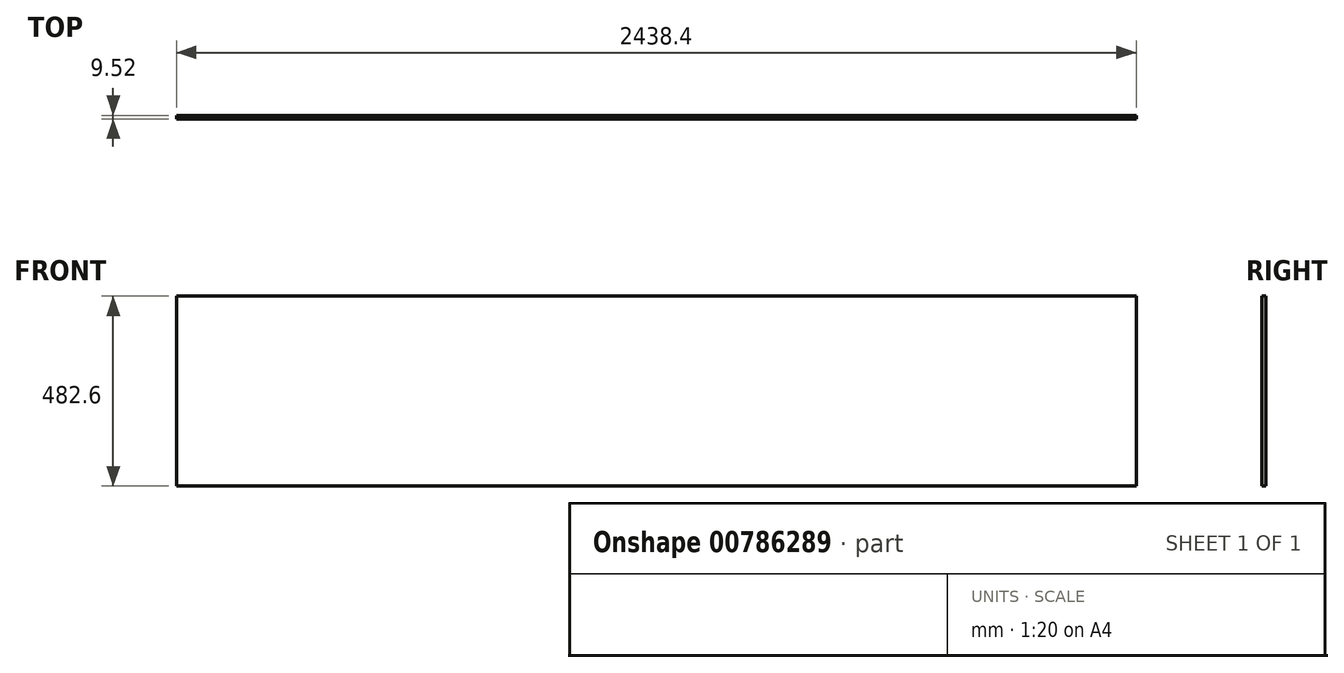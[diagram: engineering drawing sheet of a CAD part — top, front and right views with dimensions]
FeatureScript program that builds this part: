
annotation { "Feature Type Name" : "Feature", "Feature Type Description" : "" }
export const myFeature = defineFeature(function(context is Context, id is Id, definition is map)
    precondition{}
    {
        {
            var Q0;
            Q0=qCreatedBy(makeId("Front.planeOp"),FACE);
            var sketch = newSketch(context, id + "F0", { "sketchPlane" : qUnion([Q0])});
            skLineSegment(sketch, "E0.bottom", {"start": v(-1219.2, 241.3) * mm, "end": v(1219.2, 241.3) * mm});
            skLineSegment(sketch, "E0.top", {"start": v(-1219.2, -241.3) * mm, "end": v(1219.2, -241.3) * mm});
            skLineSegment(sketch, "E0.left", {"start": v(-1219.2, 241.3) * mm, "end": v(-1219.2, -241.3) * mm});
            skLineSegment(sketch, "E0.right", {"start": v(1219.2, 241.3) * mm, "end": v(1219.2, -241.3) * mm});
            skPoint(sketch, "E0.middle", {"position": v(0, 0) * mm});
            skSolve(sketch);
        }
        {
            var Q0;
            Q0=makeQuery(id+"F0.imprint","IMPRINT",FACE,{"disambiguationData":[TD([[makeQuery(id+"F0.imprint","IMPRINT",EDGE,{"derivedFrom":sQuery(id+"F0.wireOp",EDGE,"E0.bottom")}),-1.0]])]});
            extrude(context, id + "F1", {"entities" : qUnion([Q0]), "endBound" : BoundingType.SYMMETRIC, "depth" : 9.52 * mm, "offsetDistance" : 25.4 * mm});
        }
    });
